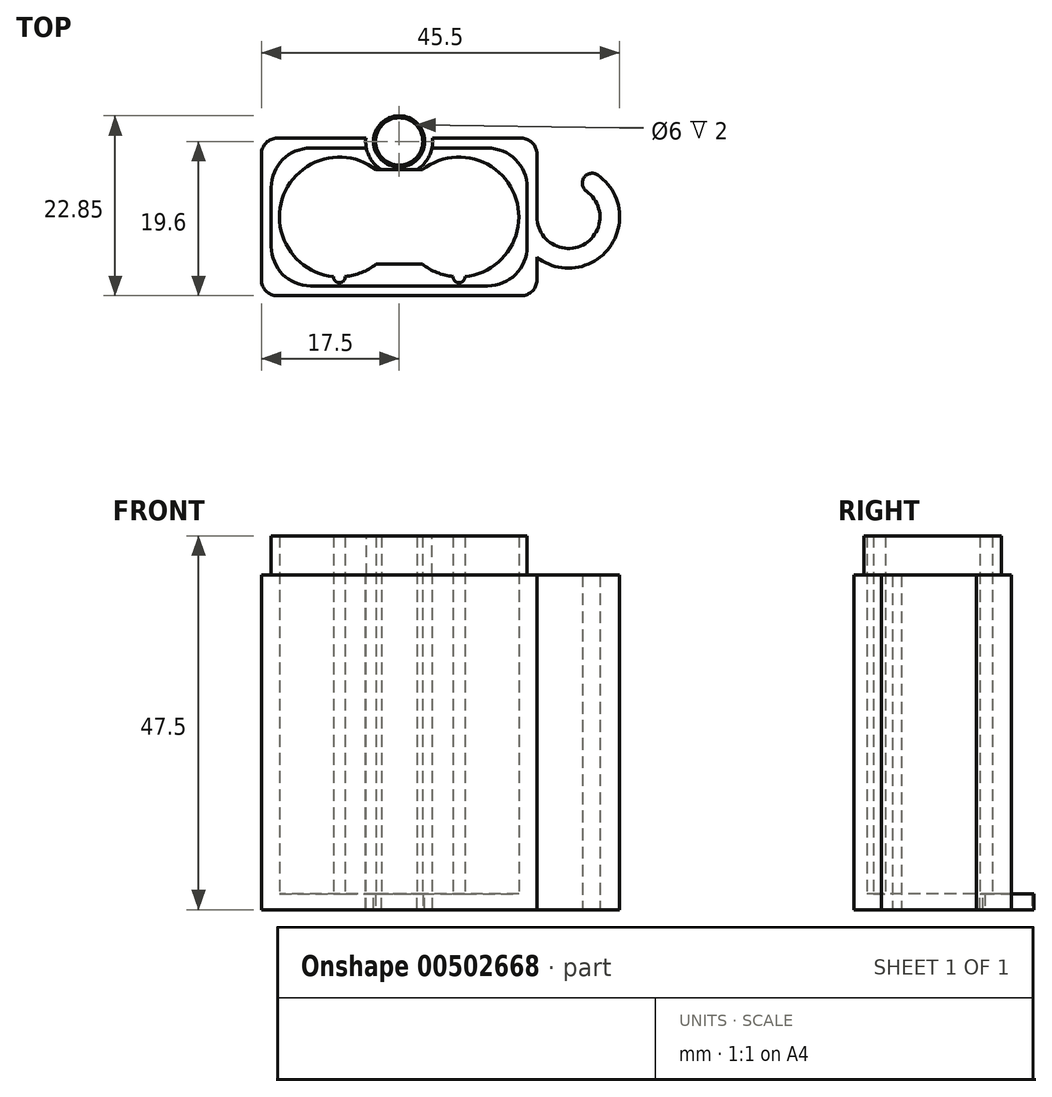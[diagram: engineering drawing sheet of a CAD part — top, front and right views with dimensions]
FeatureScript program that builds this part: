
annotation { "Feature Type Name" : "Feature", "Feature Type Description" : "" }
export const myFeature = defineFeature(function(context is Context, id is Id, definition is map)
    precondition{}
    {
        {
            var Q0;
            Q0=qCreatedBy(makeId("Top.planeOp"),FACE);
            var sketch = newSketch(context, id + "F0", { "sketchPlane" : qUnion([Q0])});
            skLineSegment(sketch, "E0", {"start": v(0, 48.4) * mm, "end": v(0, -44.37) * mm, "construction": true});
            skLineSegment(sketch, "E1", {"start": v(-7.6, 48.21) * mm, "end": v(-7.6, -44.56) * mm, "construction": true});
            skLineSegment(sketch, "E2", {"start": v(7.6, 47.25) * mm, "end": v(7.6, -45.52) * mm, "construction": true});
            skLineSegment(sketch, "E3", {"start": v(-29.15, 0) * mm, "end": v(40.62, 0) * mm, "construction": true});
            skCircle(sketch, "E4", {"center": v(-7.6, 0) * mm, "radius": 7.6 * mm});
            skCircle(sketch, "E5", {"center": v(7.6, 0) * mm, "radius": 7.6 * mm});
            skLineSegment(sketch, "E6.bottom", {"start": v(17.5, 10) * mm, "end": v(-17.5, 10) * mm});
            skLineSegment(sketch, "E6.top", {"start": v(17.5, -10) * mm, "end": v(-17.5, -10) * mm});
            skLineSegment(sketch, "E6.left", {"start": v(17.5, 10) * mm, "end": v(17.5, -10) * mm});
            skLineSegment(sketch, "E6.right", {"start": v(-17.5, 10) * mm, "end": v(-17.5, -10) * mm});
            skPoint(sketch, "E6.middle", {"position": v(0, 0) * mm});
            skLineSegment(sketch, "E7", {"start": v(-22.07, 6) * mm, "end": v(26.42, 6) * mm, "construction": true});
            skLineSegment(sketch, "E8", {"start": v(-2.94, 6) * mm, "end": v(2.94, 6) * mm});
            skLineSegment(sketch, "E9.MirrorCS", {"start": v(-29.15, 12) * mm, "end": v(40.62, 12) * mm, "construction": true});
            skLineSegment(sketch, "E10.MirrorCS", {"start": v(-2.94, -6) * mm, "end": v(2.94, -6) * mm});
            skCircle(sketch, "E11", {"center": v(0, 9.6) * mm, "radius": 3.25 * mm});
            skCircle(sketch, "E12", {"center": v(0, 9.6) * mm, "radius": 4.25 * mm});
            skCircle(sketch, "E13", {"center": v(-7.6, -7.6) * mm, "radius": 0.75 * mm});
            skCircle(sketch, "E14", {"center": v(7.6, -7.6) * mm, "radius": 0.75 * mm});
            skSolve(sketch);
        }
        {
            var Q0;
            {var subQ0=sQuery(id+"F0.wireOp",EDGE,"E12");var subQ1=sQuery(id+"F0.wireOp",EDGE,"E6.bottom");var subQ2=makeQuery(id+"F0.imprint","INTERSECT",VERTEX,{"disambiguationData":[OD(0.0)],"derivedFrom":[subQ1,subQ0]});Q0=makeQuery(id+"F0.imprint","IMPRINT",FACE,{"disambiguationData":[TD([[makeQuery(id+"F0.imprint","IMPRINT",EDGE,{"disambiguationData":[TD([[subQ2,-1.0]])],"derivedFrom":subQ1}),-1.0]])]});}
            var Q1;
            {var subQ0=sQuery(id+"F0.wireOp",EDGE,"E11");var subQ1=sQuery(id+"F0.wireOp",EDGE,"E6.bottom");var subQ2=makeQuery(id+"F0.imprint","INTERSECT",VERTEX,{"disambiguationData":[OD(0.0)],"derivedFrom":[subQ1,subQ0]});Q1=makeQuery(id+"F0.imprint","IMPRINT",FACE,{"disambiguationData":[TD([[makeQuery(id+"F0.imprint","IMPRINT",EDGE,{"disambiguationData":[TD([[subQ2,-1.0]])],"derivedFrom":subQ1}),1.0]])]});}
            var Q2;
            {var subQ0=sQuery(id+"F0.wireOp",EDGE,"E11");var subQ1=sQuery(id+"F0.wireOp",EDGE,"E6.bottom");var subQ2=makeQuery(id+"F0.imprint","INTERSECT",VERTEX,{"disambiguationData":[OD(0.0)],"derivedFrom":[subQ1,subQ0]});Q2=makeQuery(id+"F0.imprint","IMPRINT",FACE,{"disambiguationData":[TD([[makeQuery(id+"F0.imprint","IMPRINT",EDGE,{"disambiguationData":[TD([[subQ2,-1.0]])],"derivedFrom":subQ1}),-1.0]])]});}
            var Q3;
            {var subQ0=sQuery(id+"F0.wireOp",EDGE,"E8");Q3=makeQuery(id+"F0.imprint","IMPRINT",FACE,{"disambiguationData":[TD([[makeQuery(id+"F0.imprint","IMPRINT",EDGE,{"derivedFrom":subQ0}),-1.0]])]});}
            var Q4;
            {var subQ0=sQuery(id+"F0.wireOp",EDGE,"E10.MirrorCS");Q4=makeQuery(id+"F0.imprint","IMPRINT",FACE,{"disambiguationData":[TD([[makeQuery(id+"F0.imprint","IMPRINT",EDGE,{"derivedFrom":subQ0}),1.0]])]});}
            var Q5;
            {var subQ0=sQuery(id+"F0.wireOp",EDGE,"E12");var subQ1=sQuery(id+"F0.wireOp",EDGE,"E6.bottom");var subQ2=makeQuery(id+"F0.imprint","INTERSECT",VERTEX,{"disambiguationData":[OD(0.0)],"derivedFrom":[subQ1,subQ0]});Q5=makeQuery(id+"F0.imprint","IMPRINT",FACE,{"disambiguationData":[TD([[makeQuery(id+"F0.imprint","IMPRINT",EDGE,{"disambiguationData":[TD([[subQ2,-1.0]])],"derivedFrom":subQ1}),1.0]])]});}
            var Q6;
            {var subQ0=sQuery(id+"F0.wireOp",EDGE,"E4");var subQ5=makeQuery(id+"F0.imprint","INTERSECT",VERTEX,{"derivedFrom":[subQ0,sQuery(id+"F0.wireOp",EDGE,"E8")]});Q6=makeQuery(id+"F0.imprint","IMPRINT",FACE,{"disambiguationData":[TD([[makeQuery(id+"F0.imprint","IMPRINT",EDGE,{"disambiguationData":[TD([[subQ5,1.0]])],"derivedFrom":subQ0}),1.0]])]});}
            var Q7;
            {var subQ0=sQuery(id+"F0.wireOp",EDGE,"E5");var subQ1=makeQuery(id+"F0.imprint","INTERSECT",VERTEX,{"derivedFrom":[subQ0,sQuery(id+"F0.wireOp",EDGE,"E8")]});Q7=makeQuery(id+"F0.imprint","IMPRINT",FACE,{"disambiguationData":[TD([[makeQuery(id+"F0.imprint","IMPRINT",EDGE,{"disambiguationData":[TD([[subQ1,-1.0]])],"derivedFrom":subQ0}),1.0]])]});}
            var Q8;
            Q8=makeQuery(id+"F0.imprint","IMPRINT",FACE,{"disambiguationData":[TD([[makeQuery(id+"F0.imprint","IMPRINT",EDGE,{"derivedFrom":sQuery(id+"F0.wireOp",EDGE,"E6.top")}),-1.0]])]});
            var Q9;
            {var subQ0=sQuery(id+"F0.wireOp",EDGE,"E13");var subQ1=sQuery(id+"F0.wireOp",EDGE,"E4");var subQ2=makeQuery(id+"F0.imprint","INTERSECT",VERTEX,{"disambiguationData":[OD(0.0)],"derivedFrom":[subQ1,subQ0]});Q9=makeQuery(id+"F0.imprint","IMPRINT",FACE,{"disambiguationData":[TD([[makeQuery(id+"F0.imprint","IMPRINT",EDGE,{"disambiguationData":[TD([[subQ2,-1.0]])],"derivedFrom":subQ1}),1.0]])]});}
            var Q10;
            {var subQ0=sQuery(id+"F0.wireOp",EDGE,"E13");var subQ1=sQuery(id+"F0.wireOp",EDGE,"E4");var subQ2=makeQuery(id+"F0.imprint","INTERSECT",VERTEX,{"disambiguationData":[OD(0.0)],"derivedFrom":[subQ1,subQ0]});Q10=makeQuery(id+"F0.imprint","IMPRINT",FACE,{"disambiguationData":[TD([[makeQuery(id+"F0.imprint","IMPRINT",EDGE,{"disambiguationData":[TD([[subQ2,-1.0]])],"derivedFrom":subQ1}),-1.0]])]});}
            var Q11;
            {var subQ0=sQuery(id+"F0.wireOp",EDGE,"E14");var subQ1=sQuery(id+"F0.wireOp",EDGE,"E5");var subQ2=makeQuery(id+"F0.imprint","INTERSECT",VERTEX,{"disambiguationData":[OD(0.0)],"derivedFrom":[subQ1,subQ0]});Q11=makeQuery(id+"F0.imprint","IMPRINT",FACE,{"disambiguationData":[TD([[makeQuery(id+"F0.imprint","IMPRINT",EDGE,{"disambiguationData":[TD([[subQ2,-1.0]])],"derivedFrom":subQ1}),1.0]])]});}
            var Q12;
            {var subQ0=sQuery(id+"F0.wireOp",EDGE,"E14");var subQ1=sQuery(id+"F0.wireOp",EDGE,"E5");var subQ2=makeQuery(id+"F0.imprint","INTERSECT",VERTEX,{"disambiguationData":[OD(0.0)],"derivedFrom":[subQ1,subQ0]});Q12=makeQuery(id+"F0.imprint","IMPRINT",FACE,{"disambiguationData":[TD([[makeQuery(id+"F0.imprint","IMPRINT",EDGE,{"disambiguationData":[TD([[subQ2,-1.0]])],"derivedFrom":subQ1}),-1.0]])]});}
            var Q13;
            {var subQ0=sQuery(id+"F0.wireOp",EDGE,"E12");var subQ1=sQuery(id+"F0.wireOp",EDGE,"E8");var subQ2=makeQuery(id+"F0.imprint","INTERSECT",VERTEX,{"disambiguationData":[OD(0.0)],"derivedFrom":[subQ1,subQ0]});Q13=makeQuery(id+"F0.imprint","IMPRINT",FACE,{"disambiguationData":[TD([[makeQuery(id+"F0.imprint","IMPRINT",EDGE,{"disambiguationData":[TD([[subQ2,-1.0]])],"derivedFrom":subQ1}),-1.0]])]});}
            extrude(context, id + "F1", {"entities" : qUnion([Q0, Q1, Q2, Q3, Q4, Q5, Q6, Q7, Q8, Q9, Q10, Q11, Q12, Q13]), "oppositeDirection" : true, "depth" : 2 * mm});
        }
        {
            var Q0;
            Q0=makeQuery(id+"F0.imprint","IMPRINT",FACE,{"disambiguationData":[TD([[makeQuery(id+"F0.imprint","IMPRINT",EDGE,{"derivedFrom":sQuery(id+"F0.wireOp",EDGE,"E6.top")}),-1.0]])]});
            var Q1;
            {var subQ0=sQuery(id+"F0.wireOp",EDGE,"E12");var subQ1=sQuery(id+"F0.wireOp",EDGE,"E6.bottom");var subQ2=makeQuery(id+"F0.imprint","INTERSECT",VERTEX,{"disambiguationData":[OD(0.0)],"derivedFrom":[subQ1,subQ0]});Q1=makeQuery(id+"F0.imprint","IMPRINT",FACE,{"disambiguationData":[TD([[makeQuery(id+"F0.imprint","IMPRINT",EDGE,{"disambiguationData":[TD([[subQ2,-1.0]])],"derivedFrom":subQ1}),-1.0]])]});}
            var Q2;
            {var subQ0=sQuery(id+"F0.wireOp",EDGE,"E12");var subQ1=sQuery(id+"F0.wireOp",EDGE,"E6.bottom");var subQ2=makeQuery(id+"F0.imprint","INTERSECT",VERTEX,{"disambiguationData":[OD(0.0)],"derivedFrom":[subQ1,subQ0]});Q2=makeQuery(id+"F0.imprint","IMPRINT",FACE,{"disambiguationData":[TD([[makeQuery(id+"F0.imprint","IMPRINT",EDGE,{"disambiguationData":[TD([[subQ2,-1.0]])],"derivedFrom":subQ1}),1.0]])]});}
            extrude(context, id + "F2", {"entities" : qUnion([Q0, Q1, Q2]), "operationType" : NewBodyOperationType.ADD, "depth" : 45.5 * mm});
        }
        {
            var Q0;
            Q0=makeQuery(id+"F2.opExtrude","CAP_FACE",FACE,{"disambiguationData":[OSD([sQuery(id+"F0.wireOp",EDGE,"E4"),sQuery(id+"F0.wireOp",EDGE,"E5"),sQuery(id+"F0.wireOp",EDGE,"E6.bottom"),sQuery(id+"F0.wireOp",EDGE,"E6.top"),sQuery(id+"F0.wireOp",EDGE,"E6.left"),sQuery(id+"F0.wireOp",EDGE,"E6.right"),sQuery(id+"F0.wireOp",EDGE,"E8"),sQuery(id+"F0.wireOp",EDGE,"E10.MirrorCS"),sQuery(id+"F0.wireOp",EDGE,"E11"),sQuery(id+"F0.wireOp",EDGE,"E12"),sQuery(id+"F0.wireOp",EDGE,"E13"),sQuery(id+"F0.wireOp",EDGE,"E14")])],"isStart":false});
            var sketch = newSketch(context, id + "F3", { "sketchPlane" : qUnion([Q0])});
            skLineSegment(sketch, "E15.bottom", {"start": v(16.25, 8.75) * mm, "end": v(-16.25, 8.75) * mm});
            skLineSegment(sketch, "E15.top", {"start": v(16.25, -8.75) * mm, "end": v(-16.25, -8.75) * mm});
            skLineSegment(sketch, "E15.left", {"start": v(16.25, 8.75) * mm, "end": v(16.25, -8.75) * mm});
            skLineSegment(sketch, "E15.right", {"start": v(-16.25, 8.75) * mm, "end": v(-16.25, -8.75) * mm});
            skPoint(sketch, "E15.middle", {"position": v(0, 0) * mm});
            skCircle(sketch, "E16", {"center": v(0, 9.6) * mm, "radius": 3.75 * mm});
            skSolve(sketch);
        }
        {
            var Q0;
            Q0=makeQuery(id+"F3.imprint","IMPRINT",FACE,{"disambiguationData":[TD([[makeQuery(id+"F3.imprint","IMPRINT",EDGE,{"derivedFrom":sQuery(id+"F3.wireOp",EDGE,"E15.top")}),1.0]])]});
            extrude(context, id + "F4", {"entities" : qUnion([Q0]), "operationType" : NewBodyOperationType.REMOVE, "oppositeDirection" : true, "depth" : 5 * mm});
        }
        {
            var Q0;
            {var subQ0=sQuery(id+"F0.wireOp",EDGE,"E6.left");var subQ1=sQuery(id+"F0.wireOp",EDGE,"E6.top");Q0=makeQuery(id+"F2.boolean.opBoolean","MERGE",EDGE,{"derivedFrom":[makeQuery(id+"F1.opExtrude","SWEPT_EDGE",EDGE,{"disambiguationData":[OSD([subQ1,subQ0])]}),makeQuery(id+"F2.opExtrude","SWEPT_EDGE",EDGE,{"disambiguationData":[OSD([subQ1,subQ0])]})]});}
            var Q1;
            {var subQ0=sQuery(id+"F0.wireOp",EDGE,"E6.left");var subQ1=sQuery(id+"F0.wireOp",EDGE,"E6.bottom");Q1=makeQuery(id+"F2.boolean.opBoolean","MERGE",EDGE,{"derivedFrom":[makeQuery(id+"F1.opExtrude","SWEPT_EDGE",EDGE,{"disambiguationData":[OSD([subQ1,subQ0])]}),makeQuery(id+"F2.opExtrude","SWEPT_EDGE",EDGE,{"disambiguationData":[OSD([subQ1,subQ0])]})]});}
            var Q2;
            {var subQ0=sQuery(id+"F0.wireOp",EDGE,"E6.right");var subQ1=sQuery(id+"F0.wireOp",EDGE,"E6.bottom");Q2=makeQuery(id+"F2.boolean.opBoolean","MERGE",EDGE,{"derivedFrom":[makeQuery(id+"F1.opExtrude","SWEPT_EDGE",EDGE,{"disambiguationData":[OSD([subQ1,subQ0])]}),makeQuery(id+"F2.opExtrude","SWEPT_EDGE",EDGE,{"disambiguationData":[OSD([subQ1,subQ0])]})]});}
            var Q3;
            {var subQ0=sQuery(id+"F0.wireOp",EDGE,"E6.right");var subQ1=sQuery(id+"F0.wireOp",EDGE,"E6.top");Q3=makeQuery(id+"F2.boolean.opBoolean","MERGE",EDGE,{"derivedFrom":[makeQuery(id+"F1.opExtrude","SWEPT_EDGE",EDGE,{"disambiguationData":[OSD([subQ1,subQ0])]}),makeQuery(id+"F2.opExtrude","SWEPT_EDGE",EDGE,{"disambiguationData":[OSD([subQ1,subQ0])]})]});}
            fillet(context, id + "F5", {"entities" : qUnion([Q0, Q1, Q2, Q3]), "radius" : 2 * mm, "tangentPropagation" : true, "allowEdgeOverflow" : false});
        }
        {
            var Q0;
            Q0=makeQuery(id+"F4.boolean.opBoolean","COPY",EDGE,{"derivedFrom":makeQuery(id+"F4.opExtrude","SWEPT_EDGE",EDGE,{"disambiguationData":[OSD([sQuery(id+"F3.wireOp",EDGE,"E15.top"),sQuery(id+"F3.wireOp",EDGE,"E15.left")])]})});
            var Q1;
            Q1=makeQuery(id+"F4.boolean.opBoolean","COPY",EDGE,{"derivedFrom":makeQuery(id+"F4.opExtrude","SWEPT_EDGE",EDGE,{"disambiguationData":[OSD([sQuery(id+"F3.wireOp",EDGE,"E15.bottom"),sQuery(id+"F3.wireOp",EDGE,"E15.left")])]})});
            var Q2;
            Q2=makeQuery(id+"F4.boolean.opBoolean","COPY",EDGE,{"derivedFrom":makeQuery(id+"F4.opExtrude","SWEPT_EDGE",EDGE,{"disambiguationData":[OSD([sQuery(id+"F3.wireOp",EDGE,"E15.bottom"),sQuery(id+"F3.wireOp",EDGE,"E15.right")])]})});
            var Q3;
            Q3=makeQuery(id+"F4.boolean.opBoolean","COPY",EDGE,{"derivedFrom":makeQuery(id+"F4.opExtrude","SWEPT_EDGE",EDGE,{"disambiguationData":[OSD([sQuery(id+"F3.wireOp",EDGE,"E15.top"),sQuery(id+"F3.wireOp",EDGE,"E15.right")])]})});
            fillet(context, id + "F6", {"entities" : qUnion([Q0, Q1, Q2, Q3]), "radius" : 5 * mm, "tangentPropagation" : true, "allowEdgeOverflow" : false});
        }
        {
            var Q0;
            Q0=makeQuery(id+"F1.opExtrude","CAP_FACE",FACE,{"disambiguationData":[OSD([sQuery(id+"F0.wireOp",EDGE,"E6.bottom"),sQuery(id+"F0.wireOp",EDGE,"E6.top"),sQuery(id+"F0.wireOp",EDGE,"E6.left"),sQuery(id+"F0.wireOp",EDGE,"E6.right"),sQuery(id+"F0.wireOp",EDGE,"E12")])],"isStart":false});
            var sketch = newSketch(context, id + "F7", { "sketchPlane" : qUnion([Q0])});
            skLineSegment(sketch, "E17", {"start": v(-40.9, 0) * mm, "end": v(48.82, 0) * mm, "construction": true});
            skLineSegment(sketch, "E18", {"start": v(21.5, 5.85) * mm, "end": v(21.5, -6.22) * mm, "construction": true});
            skCircle(sketch, "E19", {"center": v(21.5, 0) * mm, "radius": 4 * mm});
            skCircle(sketch, "E20", {"center": v(21.5, 0) * mm, "radius": 6.5 * mm});
            skLineSegment(sketch, "E21", {"start": v(21.5, 0) * mm, "end": v(25.23, -5.32) * mm, "construction": true});
            skLineSegment(sketch, "E22", {"start": v(23.8, -3.28) * mm, "end": v(25.23, -5.32) * mm, "construction": true});
            skCircle(sketch, "E23", {"center": v(24.51, -4.3) * mm, "radius": 1.25 * mm});
            skCircle(sketch, "E24.MirrorC", {"center": v(-21.5, 0) * mm, "radius": 6.5 * mm});
            skCircle(sketch, "E25.MirrorC", {"center": v(-21.5, 0) * mm, "radius": 4 * mm});
            skCircle(sketch, "E26.MirrorC", {"center": v(-24.51, -4.3) * mm, "radius": 1.25 * mm});
            skSolve(sketch);
        }
        {
            var Q0;
            {var subQ0=sQuery(id+"F7.wireOp",EDGE,"E23");var subQ1=sQuery(id+"F7.wireOp",EDGE,"E19");var subQ2=makeQuery(id+"F7.imprint","INTERSECT",VERTEX,{"derivedFrom":[subQ1,subQ0]});Q0=makeQuery(id+"F7.imprint","IMPRINT",FACE,{"disambiguationData":[TD([[makeQuery(id+"F7.imprint","IMPRINT",EDGE,{"disambiguationData":[TD([[subQ2,-1.0]])],"derivedFrom":subQ1}),-1.0]])]});}
            var Q1;
            {var subQ0=sQuery(id+"F7.wireOp",EDGE,"E23");var subQ1=makeQuery(id+"F7.imprint","INTERSECT",VERTEX,{"derivedFrom":[sQuery(id+"F7.wireOp",EDGE,"E20"),subQ0]});Q1=makeQuery(id+"F7.imprint","IMPRINT",FACE,{"disambiguationData":[TD([[makeQuery(id+"F7.imprint","IMPRINT",EDGE,{"disambiguationData":[TD([[subQ1,1.0]])],"derivedFrom":subQ0}),1.0]])]});}
            extrude(context, id + "F8", {"entities" : qUnion([Q0, Q1]), "operationType" : NewBodyOperationType.ADD, "oppositeDirection" : true, "depth" : 42.5 * mm});
        }
        {
            var Q0;
            {var subQ0=sQuery(id+"F0.wireOp",EDGE,"E6.left");Q0=makeQuery(id+"F8.boolean.opBoolean","MERGE",FACE,{"derivedFrom":[makeQuery(id+"F1.opExtrude","CAP_FACE",FACE,{"disambiguationData":[OSD([sQuery(id+"F0.wireOp",EDGE,"E6.bottom"),sQuery(id+"F0.wireOp",EDGE,"E6.top"),subQ0,sQuery(id+"F0.wireOp",EDGE,"E6.right"),sQuery(id+"F0.wireOp",EDGE,"E12")])],"isStart":false}),makeQuery(id+"F8.opExtrude","CAP_FACE",FACE,{"disambiguationData":[OSD([subQ0,sQuery(id+"F7.wireOp",EDGE,"E19"),sQuery(id+"F7.wireOp",EDGE,"E20"),sQuery(id+"F7.wireOp",EDGE,"E23")])],"isStart":true})]});}
            var sketch = newSketch(context, id + "F9", { "sketchPlane" : qUnion([Q0])});
            skCircle(sketch, "E27", {"center": v(0, -9.6) * mm, "radius": 3 * mm});
            skSolve(sketch);
        }
        {
            var Q0;
            Q0=makeQuery(id+"F9.imprint","IMPRINT",FACE,{"disambiguationData":[TD([[makeQuery(id+"F9.imprint","IMPRINT",EDGE,{"derivedFrom":sQuery(id+"F9.wireOp",EDGE,"E27")}),1.0]])]});
            extrude(context, id + "F10", {"entities" : qUnion([Q0]), "operationType" : NewBodyOperationType.REMOVE, "endBound" : BoundingType.THROUGH_ALL, "oppositeDirection" : true, "depth" : 2 * mm});
        }
    });
